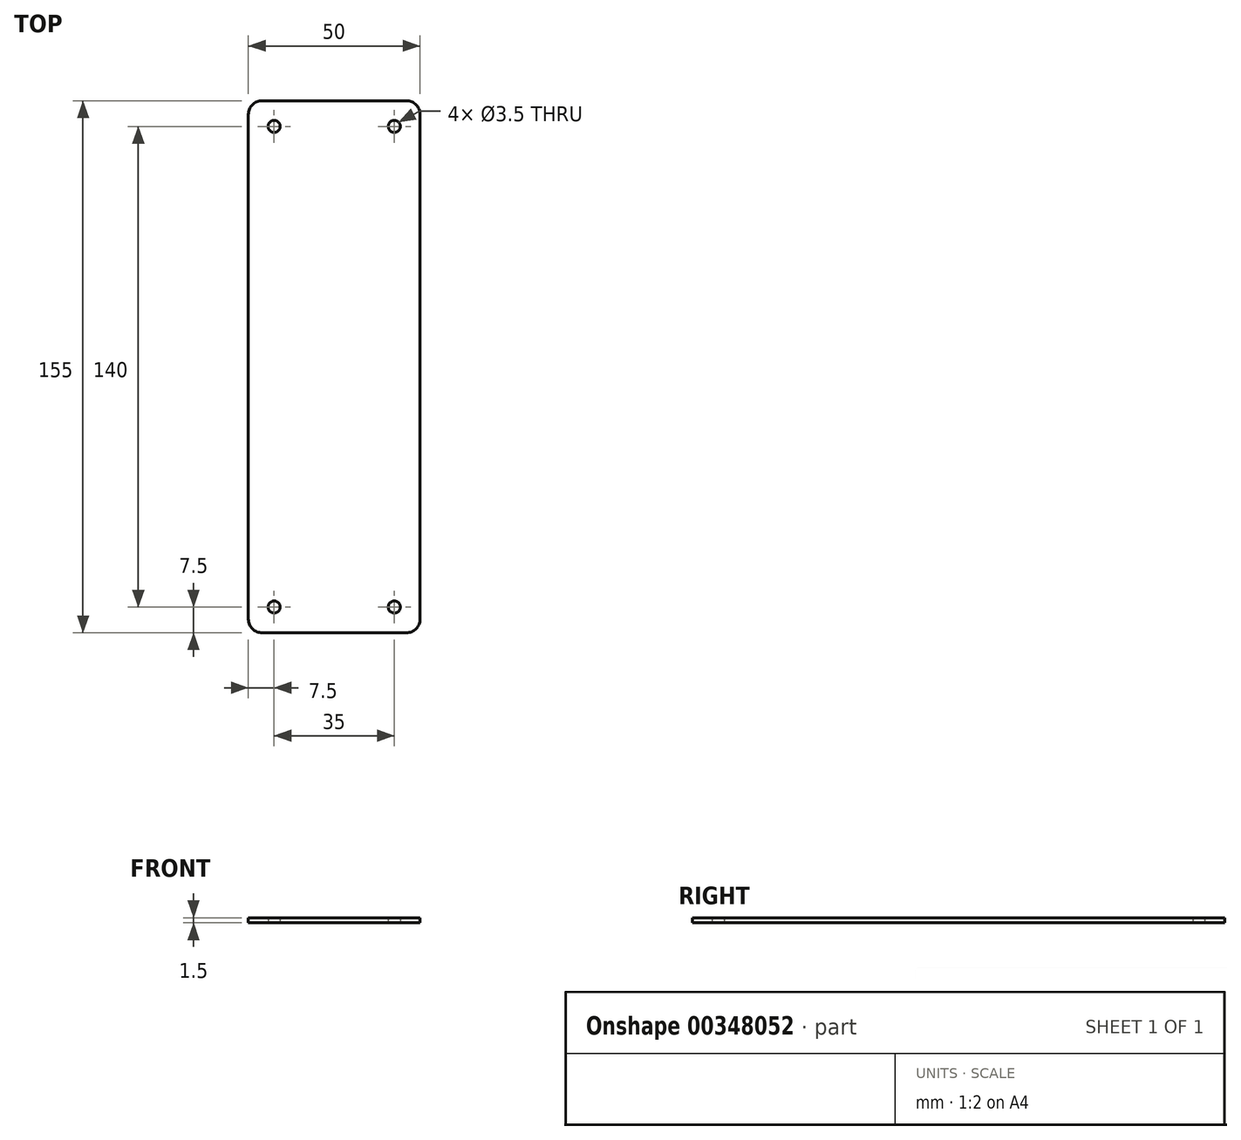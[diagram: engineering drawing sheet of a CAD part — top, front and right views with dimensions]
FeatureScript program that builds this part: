
annotation { "Feature Type Name" : "Feature", "Feature Type Description" : "" }
export const myFeature = defineFeature(function(context is Context, id is Id, definition is map)
    precondition{}
    {
        {
            var Q0;
            Q0=qCreatedBy(makeId("Top.planeOp"),FACE);
            var sketch = newSketch(context, id + "F0", { "sketchPlane" : qUnion([Q0])});
            skLineSegment(sketch, "E0.bottom", {"start": v(-21, 77.5) * mm, "end": v(21, 77.5) * mm});
            skLineSegment(sketch, "E0.top", {"start": v(-21, -77.5) * mm, "end": v(21, -77.5) * mm});
            skLineSegment(sketch, "E0.left", {"start": v(-25, 73.5) * mm, "end": v(-25, -73.5) * mm});
            skLineSegment(sketch, "E0.right", {"start": v(25, 73.5) * mm, "end": v(25, -73.5) * mm});
            skPoint(sketch, "E0.middle", {"position": v(0, 0) * mm});
            skPoint(sketch, "E1.visualSharp", {"position": v(-25, 77.5) * mm});
            skArc(sketch, "E1.filletArc", {"start": v(-21, 77.5) * mm, "mid": v(-23.83, 76.33) * mm, "end": v(-25, 73.5) * mm});
            skPoint(sketch, "E2.visualSharp", {"position": v(-25, -77.5) * mm});
            skArc(sketch, "E2.filletArc", {"start": v(-25, -73.5) * mm, "mid": v(-23.83, -76.33) * mm, "end": v(-21, -77.5) * mm});
            skPoint(sketch, "E3.visualSharp", {"position": v(25, 77.5) * mm});
            skArc(sketch, "E3.filletArc", {"start": v(25, 73.5) * mm, "mid": v(23.83, 76.33) * mm, "end": v(21, 77.5) * mm});
            skPoint(sketch, "E4.visualSharp", {"position": v(25, -77.5) * mm});
            skArc(sketch, "E4.filletArc", {"start": v(21, -77.5) * mm, "mid": v(23.83, -76.33) * mm, "end": v(25, -73.5) * mm});
            skCircle(sketch, "E5", {"center": v(-17.5, 70) * mm, "radius": 1.75 * mm});
            skLineSegment(sketch, "E6", {"start": v(-17.5, 70) * mm, "end": v(-25, 70) * mm, "construction": true});
            skCircle(sketch, "E7.MirrorC", {"center": v(17.5, 70) * mm, "radius": 1.75 * mm});
            skCircle(sketch, "E8.MirrorC", {"center": v(17.5, -70) * mm, "radius": 1.75 * mm});
            skCircle(sketch, "E9.MirrorC", {"center": v(-17.5, -70) * mm, "radius": 1.75 * mm});
            skSolve(sketch);
        }
        {
            var Q0;
            Q0=makeQuery(id+"F0.imprint","IMPRINT",FACE,{"disambiguationData":[TD([[makeQuery(id+"F0.imprint","IMPRINT",EDGE,{"derivedFrom":sQuery(id+"F0.wireOp",EDGE,"E0.bottom")}),-1.0]])]});
            extrude(context, id + "F1", {"entities" : qUnion([Q0]), "depth" : 1.5 * mm});
        }
    });
